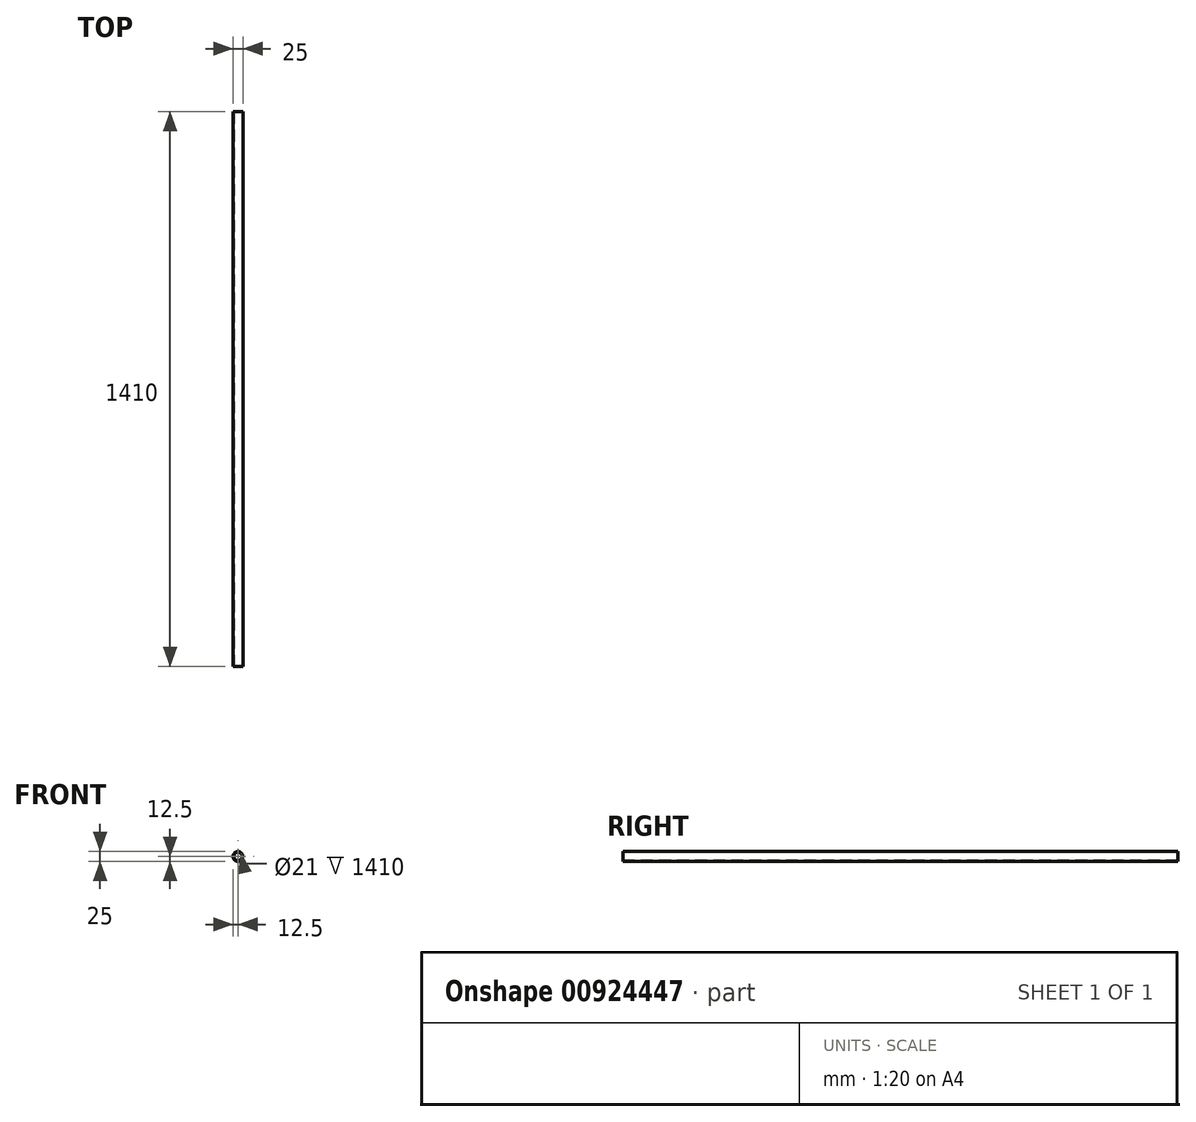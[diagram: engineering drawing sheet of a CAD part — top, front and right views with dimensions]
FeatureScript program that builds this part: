
annotation { "Feature Type Name" : "Feature", "Feature Type Description" : "" }
export const myFeature = defineFeature(function(context is Context, id is Id, definition is map)
    precondition{}
    {
        {
            var Q0;
            Q0=qCreatedBy(makeId("Front.planeOp"),FACE);
            var sketch = newSketch(context, id + "F0", { "sketchPlane" : qUnion([Q0])});
            skCircle(sketch, "E0", {"center": v(0, 0) * mm, "radius": 12.5 * mm});
            skSolve(sketch);
        }
        {
            var Q0;
            Q0=qSketchRegion(id+"F0",true);
            extrude(context, id + "F1", {"entities" : qUnion([Q0]), "depth" : 1410 * mm, "offsetDistance" : 25 * mm});
        }
        {
            var Q0;
            Q0=makeQuery(id+"F1.opExtrude","CAP_FACE",FACE,{"disambiguationData":[OSD([sQuery(id+"F0.wireOp",EDGE,"E0")])],"isStart":false});
            var sketch = newSketch(context, id + "F2", { "sketchPlane" : qUnion([Q0])});
            skCircle(sketch, "E1", {"center": v(0, 0) * mm, "radius": 10.5 * mm});
            skSolve(sketch);
        }
        {
            var Q0;
            Q0=qSketchRegion(id+"F2",true);
            extrude(context, id + "F3", {"entities" : qUnion([Q0]), "operationType" : NewBodyOperationType.REMOVE, "oppositeDirection" : true, "depth" : 2000 * mm, "offsetDistance" : 25 * mm});
        }
    });
